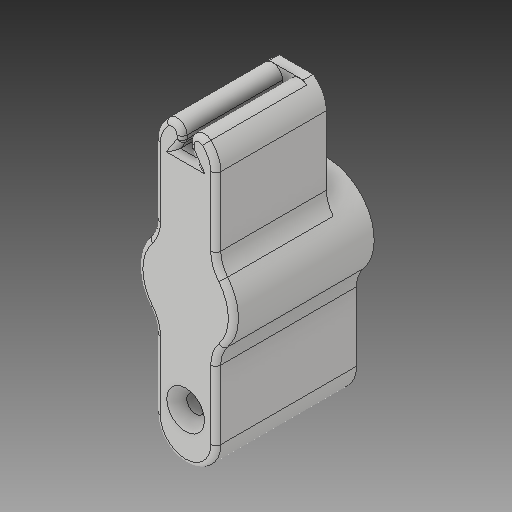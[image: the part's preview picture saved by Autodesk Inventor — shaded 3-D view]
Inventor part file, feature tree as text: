
AUTODESK INVENTOR PART (.ipt)
format: ipt  version: 2019 (Build 230136000, 136)  size: 308,736 bytes
history: native  units: mm
features: fillet x7, extrude x6, sketch x6, chamfer x1, mirror x1
ambient origin geometry x8: Origin, YZ Plane, XZ Plane, XY Plane, X Axis, Y Axis, Z Axis, Center Point
bodies: Solid1 (feature_tree)
feature tree (21):
  extrude  "Extrusion1"  Depth=4.0mm
  extrude  "Extrusion2"  Depth=2.0mm
  extrude  "Extrusion3"  Depth=9.5mm
  fillet  "Fillet1"  Radius=0.1mm
  fillet  "Fillet2"  Radius=6.0mm
  extrude  "Extrusion4"  TaperAngle=0.0deg  [1 undecoded]
  fillet  "Fillet3"  Radius=3.5mm
  fillet  "Fillet4"  Radius=3.5mm
  chamfer  "Chamfer1"  Distance=22.0mm
  fillet  "Fillet5"  Radius=53.0mm
  extrude  "Extrusion5"  Depth=12.0mm
  mirror  "Mirror1"
  extrude  "Extrusion6"  Depth=22.0mm TaperAngle=0.0deg
  fillet  "Fillet6"  Radius=6.0mm
  fillet  "Fillet7"  Radius=6.0mm
  sketch  "Sketch1"  dims[d0=31.0mm d1=4.0mm]
  sketch  "Sketch2"  dims[d2=7.5mm d3=2.0mm]
  sketch  "Sketch4"  dims[d4=2.0mm d5=9.5mm d6=0.1mm d7=6.0mm d8=0.0mm]
  sketch  "Sketch5"  dims[d9=31.0mm d10=4.0mm d11=7.5mm d12=2.0mm d13=2.0mm d14=9.5mm d15=0.1mm d16=6.0mm d17=0.0mm d19=3.5mm d21=3.5mm d22=22.0mm d23=0.0mm d48=53.0mm]
  sketch  "Sketch6"  dims[d49=15.0mm d50=12.0mm]
  sketch  "Sketch7"  dims[d51=30.0mm d52=22.0mm d53=0.0mm d54=6.0mm d55=6.0mm d56=0.7mm d57=0.7mm d58=20.0mm d59=0.0mm d60=2.0mm d61=1.0mm d62=2.0mm d63=2.0mm d64=45.0deg d65=8.0mm d66=5.0mm d67=7.0mm d68=2.5mm d69=6.0mm d70=0.0mm d71=5.0mm d72=2.0mm d73=5.0mm d74=2.0mm d75=6.0mm d76=0.0mm d77=2.0mm d78=2.0mm d79=1.0mm d80=1.0mm]
note: 1 required parameter value undecoded (feature->parameter linkage not recoverable at this tier; creation-order binding heuristic only, values carry confidence <= 0.55)
